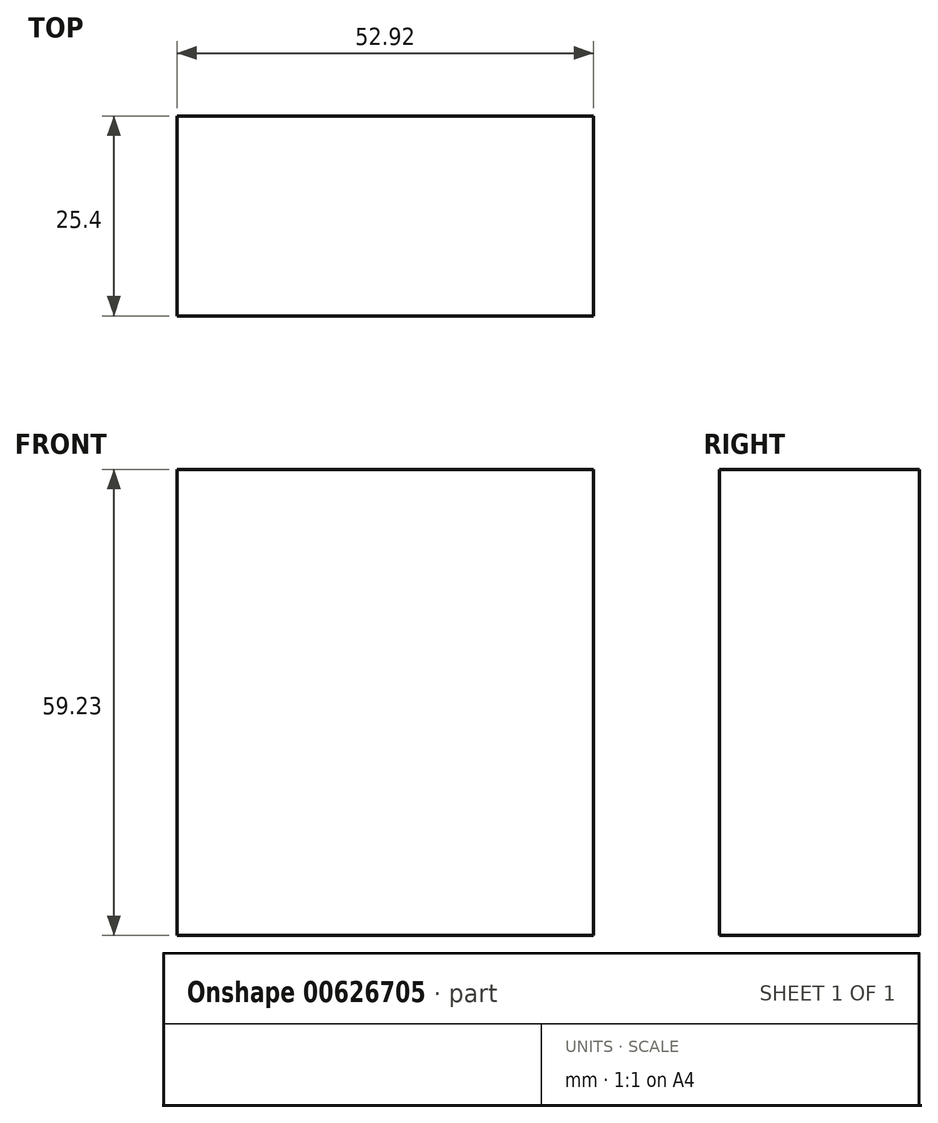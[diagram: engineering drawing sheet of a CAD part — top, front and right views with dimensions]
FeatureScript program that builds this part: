
annotation { "Feature Type Name" : "Feature", "Feature Type Description" : "" }
export const myFeature = defineFeature(function(context is Context, id is Id, definition is map)
    precondition{}
    {
        {
            var Q0;
            Q0=qCreatedBy(makeId("Front.planeOp"),FACE);
            var sketch = newSketch(context, id + "F0", { "sketchPlane" : qUnion([Q0])});
            skLineSegment(sketch, "E0.bottom", {"start": v(-52.92, 59.23) * mm, "end": v(0, 59.23) * mm});
            skLineSegment(sketch, "E0.top", {"start": v(-52.92, 0) * mm, "end": v(0, 0) * mm});
            skLineSegment(sketch, "E0.left", {"start": v(-52.92, 59.23) * mm, "end": v(-52.92, 0) * mm});
            skLineSegment(sketch, "E0.right", {"start": v(0, 59.23) * mm, "end": v(0, 0) * mm});
            skSolve(sketch);
        }
        {
            var Q0;
            Q0=makeQuery(id+"F0.imprint","IMPRINT",FACE,{"disambiguationData":[TD([[makeQuery(id+"F0.imprint","IMPRINT",EDGE,{"derivedFrom":sQuery(id+"F0.wireOp",EDGE,"E0.bottom")}),-1.0]])]});
            extrude(context, id + "F1", {"entities" : qUnion([Q0]), "depth" : 25.4 * mm, "offsetDistance" : 25.4 * mm});
        }
    });
